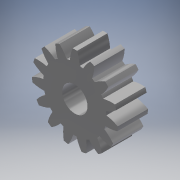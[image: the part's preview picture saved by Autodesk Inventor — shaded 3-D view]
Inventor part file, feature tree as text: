
AUTODESK INVENTOR PART (.ipt)
format: ipt  version: 2019 (Build 230136000, 136)  size: 212,992 bytes
history: native  units: mm (DEFAULTED — no unit token found)
features: plane x3, other x3, sketch x3, extrude x1, hole x1
ambient origin geometry x8: Origin, YZ Plane, XZ Plane, XY Plane, X Axis, Y Axis, Z Axis, Center Point
bodies: Solid1 (feature_tree)
feature tree (11):
  extrude  "Extrusion1"  Depth=3.0mm TaperAngle=0.0deg
  plane  "Work Plane2"
  plane  "Work Plane8"
  plane  "Work Plane9"
  other  "Przekładnia walcowa"
  hole  "Otwór1"  [1 undecoded]
  sketch  "Sketch1"  dims[d0=8.5mm d1=3.0mm d2=0.0mm]
  sketch  "Sketch2"  dims[d3=7.5mm d4=10.0mm d5=0.0mm d16=13.75mm d17=0.0mm d34=2.094395mm d39=0.0mm d41=0.0mm d43=13.75mm d46=13.75mm d47=0.0mm d48=0.0mm d49=2.5mm d50=6.0mm d51=4.0mm d52=2.0mm d53=90.0deg d54=8.0mm d55=20.594885mm]
  other  "Srf1"
  sketch  "Szkic3"
  other  "Średnica podziałowa"
note: 1 required parameter value undecoded (feature->parameter linkage not recoverable at this tier; creation-order binding heuristic only, values carry confidence <= 0.55)
